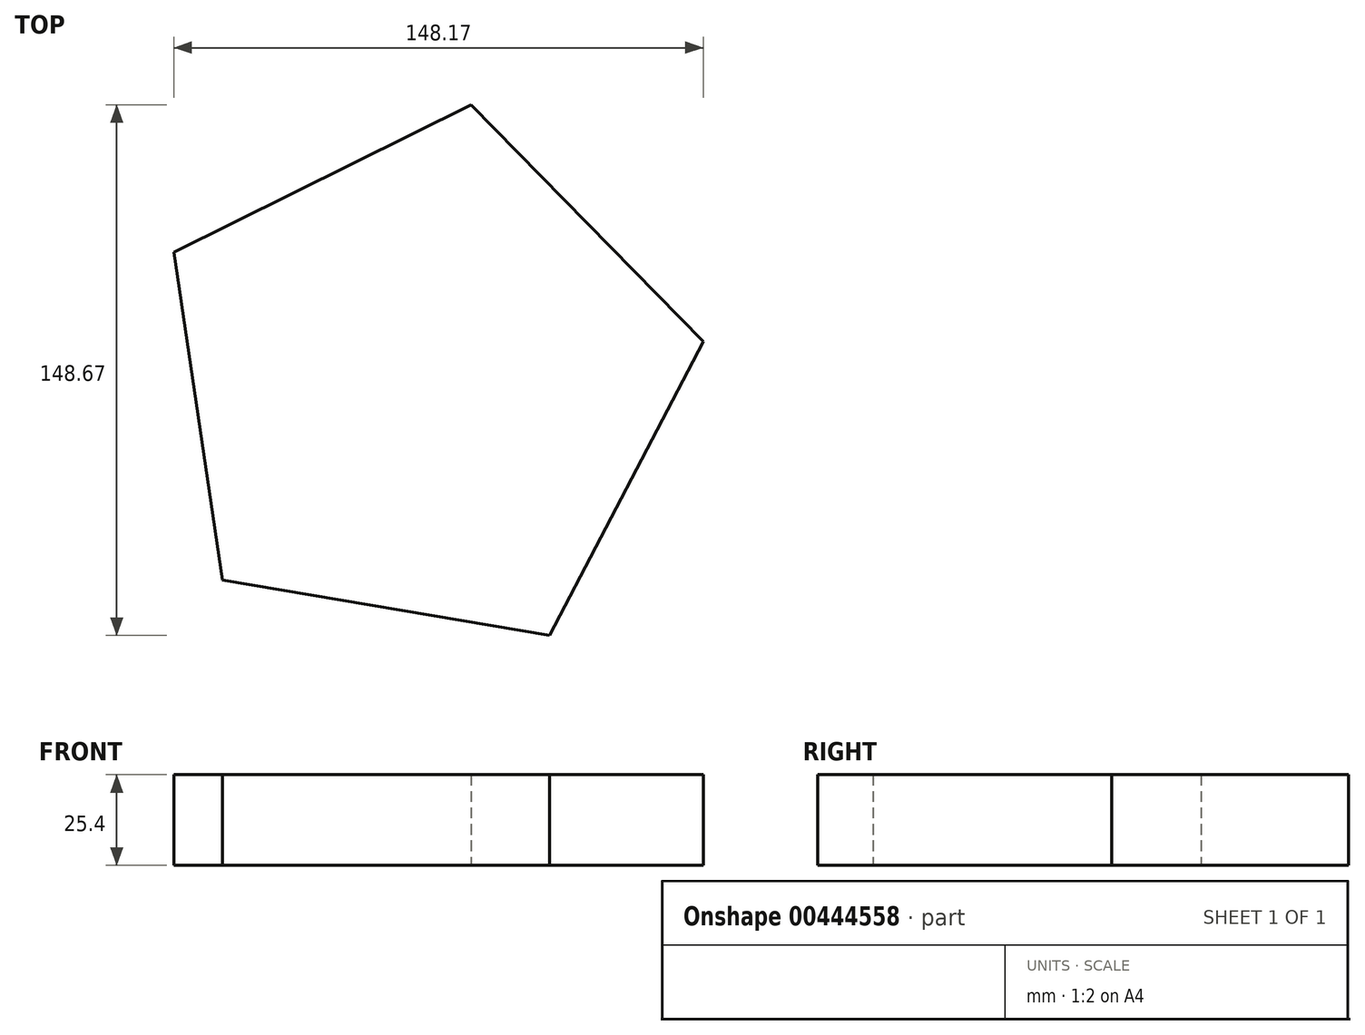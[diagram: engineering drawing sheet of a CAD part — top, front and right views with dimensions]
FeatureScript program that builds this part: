
annotation { "Feature Type Name" : "Feature", "Feature Type Description" : "" }
export const myFeature = defineFeature(function(context is Context, id is Id, definition is map)
    precondition{}
    {
        {
            var Q0;
            Q0=qCreatedBy(makeId("Top.planeOp"),FACE);
            var sketch = newSketch(context, id + "F0", { "sketchPlane" : qUnion([Q0])});
            skCircle(sketch, "E0.cCircle", {"center": v(0, 0) * mm, "radius": 63.92 * mm, "construction": true});
            skLineSegment(sketch, "E0.0", {"start": v(-70.01, 36.6) * mm, "end": v(13.18, 77.9) * mm});
            skLineSegment(sketch, "E0.1", {"start": v(13.18, 77.9) * mm, "end": v(78.16, 11.54) * mm});
            skLineSegment(sketch, "E0.2", {"start": v(78.16, 11.54) * mm, "end": v(35.12, -70.77) * mm});
            skLineSegment(sketch, "E0.3", {"start": v(35.12, -70.77) * mm, "end": v(-56.45, -55.27) * mm});
            skLineSegment(sketch, "E0.4", {"start": v(-56.45, -55.27) * mm, "end": v(-70.01, 36.6) * mm});
            skPoint(sketch, "E0.0.midPoint", {"position": v(-28.42, 57.25) * mm});
            skSolve(sketch);
        }
        {
            var Q0;
            Q0=makeQuery(id+"F0.imprint","IMPRINT",FACE,{"disambiguationData":[TD([[makeQuery(id+"F0.imprint","IMPRINT",EDGE,{"derivedFrom":sQuery(id+"F0.wireOp",EDGE,"E0.0")}),-1.0]])]});
            extrude(context, id + "F1", {"entities" : qUnion([Q0]), "depth" : 25.4 * mm});
        }
    });
